# Revit family: ALN
name_source: partatom
category: Lighting Fixtures
revit_build: Autodesk Revit 2014 (Build: 20130308_1515(x64)
units: mm (PartAtom-declared; Revit-internal decimal feet)

## types (1)
- ALN
    Apparent Load = 62 VA
    Assembly Code = D5020200
    Body Material = Paint - Hubbell - Carbon Black
    Color Filter = 16777215
    Default Elevation = 0"
    Description = Cast Aluminum Bollard
    Dimming Lamp Color Temperature Shift = <None>
    Emit Shape Visible in Rendering = No
    Emit from Circle Diameter = 6"
    Glass Material = Glass- Lighting-Clear
    Lamp = METAL HALIDE / HIGH PRESSURE SODIUM
    Load Classification = Lighting
    Manufacturer = Architectural Area Lighting
    MasterFormat Title = Parking Lighting, Roadway Lighting, Site Lighting
    Model = ALN380/481
    Number of Poles = 1
    OmniClass Number = 23.80.70.14.11.11
    OmniClass Title = Lighting Bollard
    Photometric Notes = More IES files download on Photometric Web Link
    Photometric Web File = ALN480W.IES
    Photometric Web Link = https://www.hubbell.com
    Product Documentation Link = https://hubbellcdn.com
    Product Page URL = https://www.hubbell.com
    Series = Spectra Bollard
    Shaft Height = 42"
    Tilt Angle = 90.00°
    Type Comments = Lighting Fixture
    URL = https://www.hubbell.com
    Voltage = 120 V
    Warranty = Limited 5 Years Warranty
    Wattage Comments = 62W
    Width = 7 1/2"

## geometry (parser evidence)
native form markers: Blend x12, Sweep x1
no freeform markers — native parametric forms only
